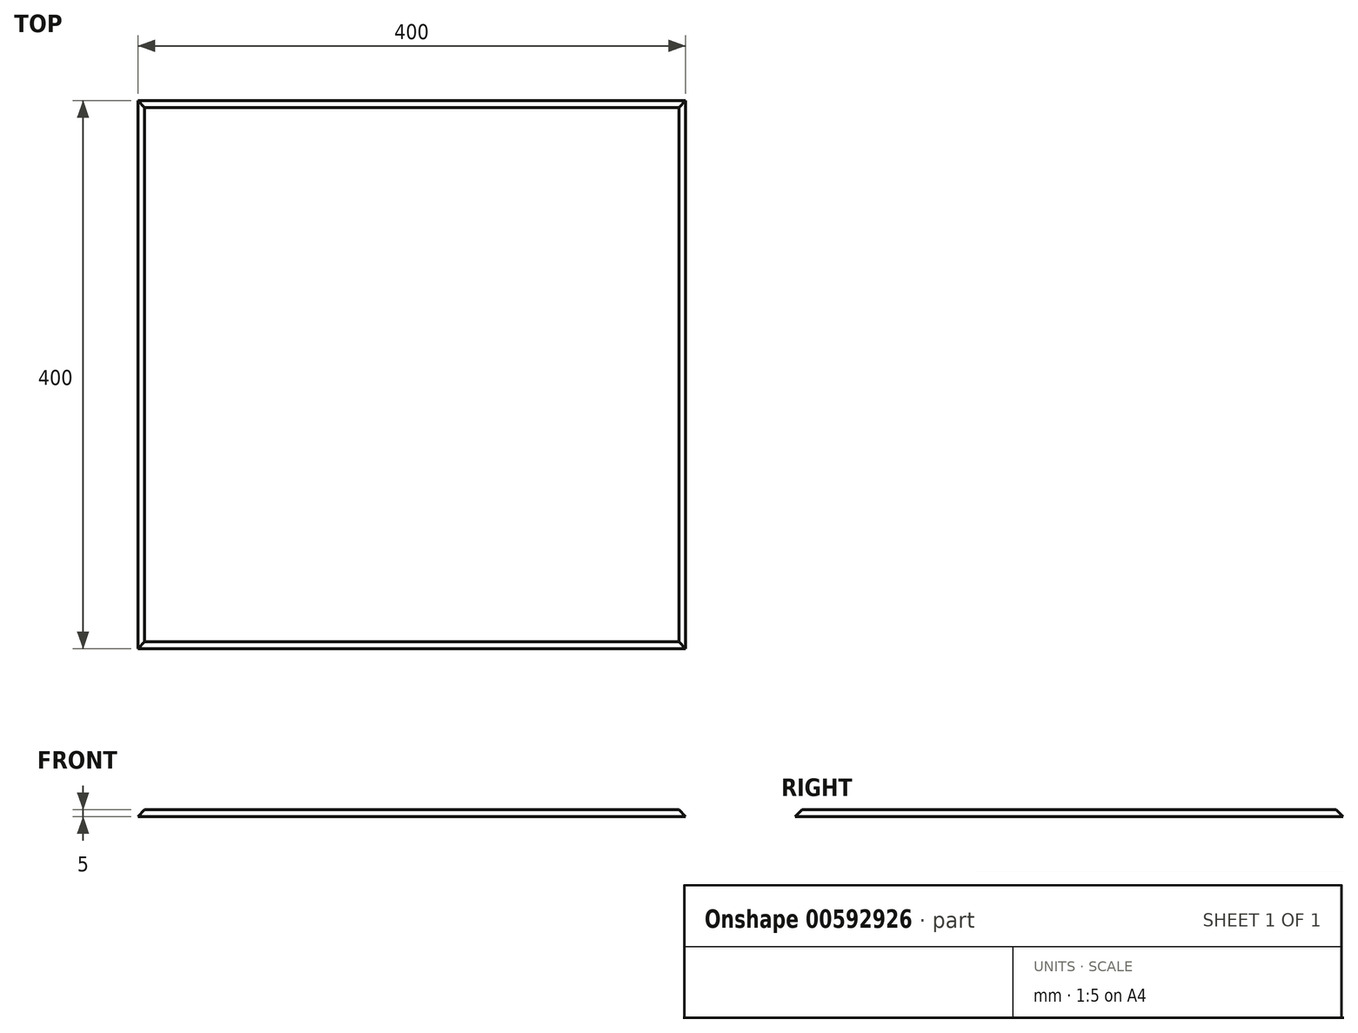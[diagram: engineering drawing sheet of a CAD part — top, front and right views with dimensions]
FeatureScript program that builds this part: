
annotation { "Feature Type Name" : "Feature", "Feature Type Description" : "" }
export const myFeature = defineFeature(function(context is Context, id is Id, definition is map)
    precondition{}
    {
        {
            var Q0;
            Q0=qCreatedBy(makeId("Top.planeOp"),FACE);
            var sketch = newSketch(context, id + "F0", { "sketchPlane" : qUnion([Q0])});
            skLineSegment(sketch, "E0.bottom", {"start": v(-199.82, 172.3) * mm, "end": v(200.18, 172.3) * mm});
            skLineSegment(sketch, "E0.top", {"start": v(-199.82, -227.7) * mm, "end": v(200.18, -227.7) * mm});
            skLineSegment(sketch, "E0.left", {"start": v(-199.82, 172.3) * mm, "end": v(-199.82, -227.7) * mm});
            skLineSegment(sketch, "E0.right", {"start": v(200.18, 172.3) * mm, "end": v(200.18, -227.7) * mm});
            skSolve(sketch);
        }
        {
            var Q0;
            Q0=makeQuery(id+"F0.imprint","IMPRINT",FACE,{"disambiguationData":[TD([[makeQuery(id+"F0.imprint","IMPRINT",EDGE,{"derivedFrom":sQuery(id+"F0.wireOp",EDGE,"E0.bottom")}),-1.0]])]});
            extrude(context, id + "F1", {"entities" : qUnion([Q0]), "depth" : 5 * mm, "offsetDistance" : 25 * mm, "hasDraft" : true, "draftAngle" : 45 * degree, "draftPullDirection" : true});
        }
    });
